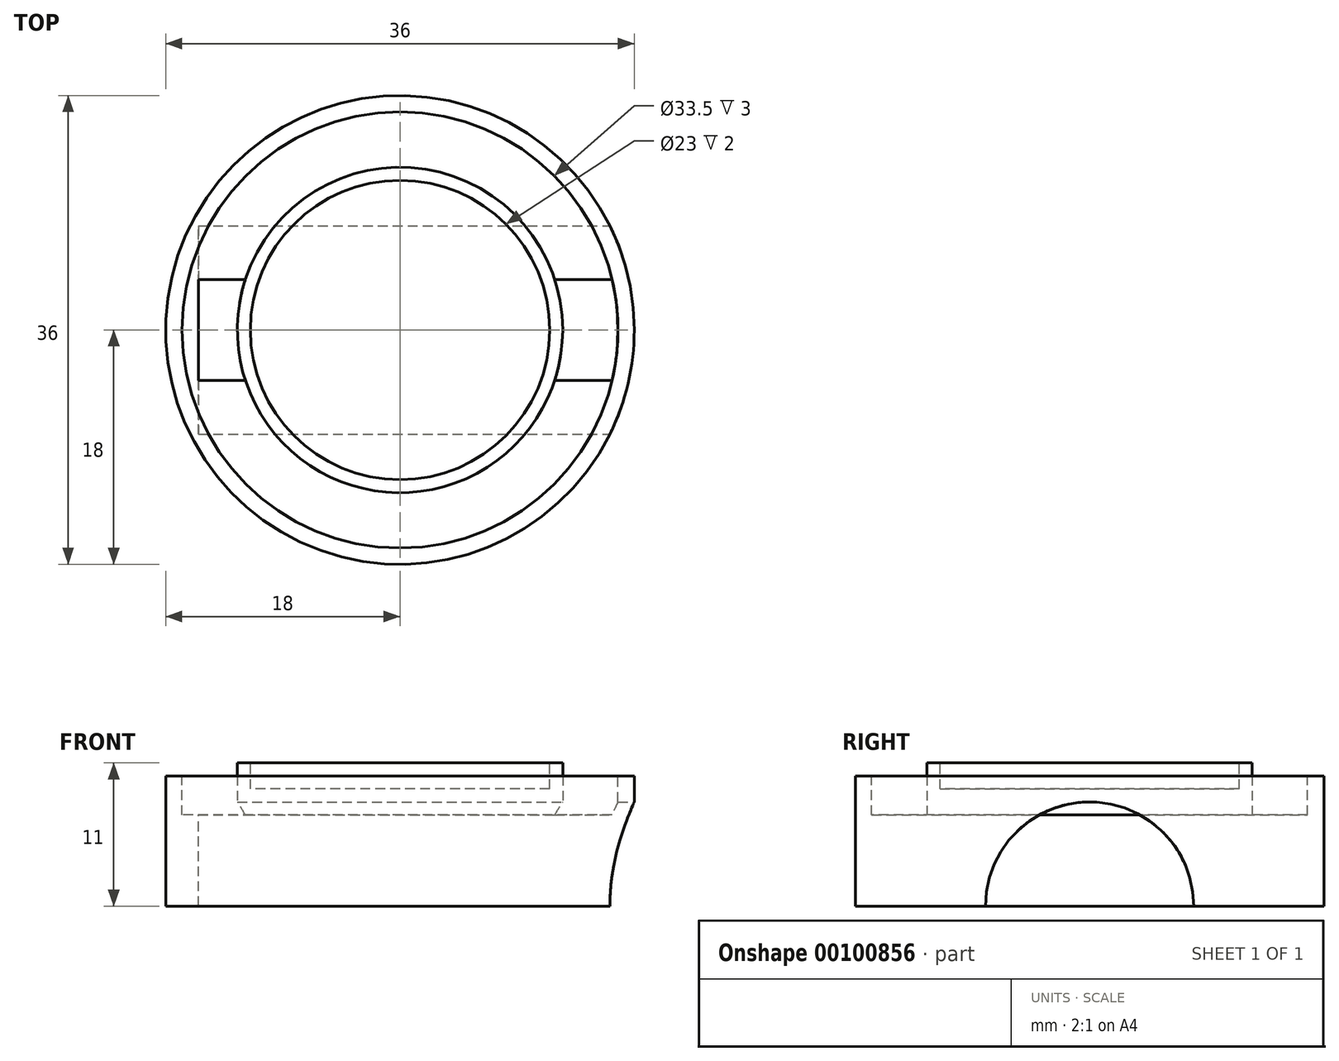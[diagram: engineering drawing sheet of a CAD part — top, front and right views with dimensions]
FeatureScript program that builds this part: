
annotation { "Feature Type Name" : "Feature", "Feature Type Description" : "" }
export const myFeature = defineFeature(function(context is Context, id is Id, definition is map)
    precondition{}
    {
        {
            var Q0;
            Q0=qCreatedBy(makeId("Top.planeOp"),FACE);
            var sketch = newSketch(context, id + "F0", { "sketchPlane" : qUnion([Q0])});
            skCircle(sketch, "E0", {"center": v(0, 0) * mm, "radius": 18 * mm});
            skCircle(sketch, "E1", {"center": v(0, 0) * mm, "radius": 16.75 * mm});
            skCircle(sketch, "E2", {"center": v(0, 0) * mm, "radius": 12.5 * mm});
            skCircle(sketch, "E3", {"center": v(0, 0) * mm, "radius": 11.5 * mm});
            skSolve(sketch);
        }
        {
            var Q0;
            Q0=makeQuery(id+"F0.imprint","IMPRINT",FACE,{"disambiguationData":[TD([[makeQuery(id+"F0.imprint","IMPRINT",EDGE,{"derivedFrom":sQuery(id+"F0.wireOp",EDGE,"E0")}),1.0]])]});
            var Q1;
            Q1=makeQuery(id+"F0.imprint","IMPRINT",FACE,{"disambiguationData":[TD([[makeQuery(id+"F0.imprint","IMPRINT",EDGE,{"derivedFrom":sQuery(id+"F0.wireOp",EDGE,"E1")}),1.0]])]});
            var Q2;
            Q2=makeQuery(id+"F0.imprint","IMPRINT",FACE,{"disambiguationData":[TD([[makeQuery(id+"F0.imprint","IMPRINT",EDGE,{"derivedFrom":sQuery(id+"F0.wireOp",EDGE,"E3")}),1.0]])]});
            var Q3;
            Q3=makeQuery(id+"F0.imprint","IMPRINT",FACE,{"disambiguationData":[TD([[makeQuery(id+"F0.imprint","IMPRINT",EDGE,{"derivedFrom":sQuery(id+"F0.wireOp",EDGE,"E2")}),1.0]])]});
            extrude(context, id + "F1", {"entities" : qUnion([Q0, Q1, Q2, Q3]), "depth" : 10 * mm});
        }
        {
            var Q0;
            Q0=makeQuery(id+"F1.opExtrude","CAP_FACE",FACE,{"disambiguationData":[OSD([sQuery(id+"F0.wireOp",EDGE,"E0")])],"isStart":false});
            var sketch = newSketch(context, id + "F2", { "sketchPlane" : qUnion([Q0])});
            skCircle(sketch, "E4", {"center": v(0, 0) * mm, "radius": 16.75 * mm});
            skSolve(sketch);
        }
        {
            var Q0;
            Q0=makeQuery(id+"F2.imprint","IMPRINT",FACE,{"disambiguationData":[TD([[makeQuery(id+"F2.imprint","IMPRINT",EDGE,{"derivedFrom":sQuery(id+"F2.wireOp",EDGE,"E4")}),1.0]])]});
            extrude(context, id + "F3", {"entities" : qUnion([Q0]), "operationType" : NewBodyOperationType.REMOVE, "oppositeDirection" : true, "depth" : 3 * mm});
        }
        {
            var Q0;
            Q0=makeQuery(id+"F3.boolean.opBoolean","COPY",FACE,{"derivedFrom":makeQuery(id+"F3.opExtrude","CAP_FACE",FACE,{"disambiguationData":[OSD([sQuery(id+"F2.wireOp",EDGE,"E4")])],"isStart":false})});
            var sketch = newSketch(context, id + "F4", { "sketchPlane" : qUnion([Q0])});
            skCircle(sketch, "E5", {"center": v(0, 0) * mm, "radius": 12.5 * mm});
            skSolve(sketch);
        }
        {
            var Q0;
            Q0=makeQuery(id+"F4.imprint","IMPRINT",FACE,{"disambiguationData":[TD([[makeQuery(id+"F4.imprint","IMPRINT",EDGE,{"derivedFrom":sQuery(id+"F4.wireOp",EDGE,"E5")}),1.0]])]});
            var Q1;
            Q1=sQuery(id+"F4.wireOp",EDGE,"E5");
            extrude(context, id + "F5", {"entities" : qUnion([Q0]), "operationType" : NewBodyOperationType.ADD, "surfaceEntities" : qUnion([Q1]), "depth" : 4 * mm});
        }
        {
            var Q0;
            Q0=makeQuery(id+"F5.opExtrude","CAP_FACE",FACE,{"disambiguationData":[OSD([sQuery(id+"F4.wireOp",EDGE,"E5")])],"isStart":false});
            var sketch = newSketch(context, id + "F6", { "sketchPlane" : qUnion([Q0])});
            skCircle(sketch, "E6", {"center": v(0, 0) * mm, "radius": 11.5 * mm});
            skSolve(sketch);
        }
        {
            var Q0;
            Q0=makeQuery(id+"F6.imprint","IMPRINT",FACE,{"disambiguationData":[TD([[makeQuery(id+"F6.imprint","IMPRINT",EDGE,{"derivedFrom":sQuery(id+"F6.wireOp",EDGE,"E6")}),1.0]])]});
            extrude(context, id + "F7", {"entities" : qUnion([Q0]), "operationType" : NewBodyOperationType.REMOVE, "oppositeDirection" : true, "depth" : 2 * mm});
        }
        {
            var Q0;
            Q0=qCreatedBy(makeId("Right.planeOp"),FACE);
            cPlane(context, id + "F8", {"entities" : qUnion([Q0]), "cplaneType" : CPlaneType.OFFSET, "offset" : 18 * mm, "width" : 150 * mm, "height" : 150 * mm});
        }
        {
            var Q0;
            Q0=qCreatedBy(id+"F8.planeOp",FACE);
            var sketch = newSketch(context, id + "F9", { "sketchPlane" : qUnion([Q0])});
            skCircle(sketch, "E7", {"center": v(0, 0) * mm, "radius": 8 * mm});
            skSolve(sketch);
        }
        {
            var Q0;
            Q0=makeQuery(id+"F9.imprint","IMPRINT",FACE,{"disambiguationData":[TD([[makeQuery(id+"F9.imprint","IMPRINT",EDGE,{"derivedFrom":sQuery(id+"F9.wireOp",EDGE,"E7")}),1.0]])]});
            extrude(context, id + "F10", {"entities" : qUnion([Q0]), "operationType" : NewBodyOperationType.REMOVE, "oppositeDirection" : true, "depth" : 33.5 * mm});
        }
        {
            var Q0;
            Q0=qCreatedBy(id+"F8.planeOp",FACE);
            cPlane(context, id + "F11", {"entities" : qUnion([Q0]), "cplaneType" : CPlaneType.OFFSET, "offset" : 1 * mm, "oppositeDirection" : true, "width" : 150 * mm, "height" : 150 * mm});
        }
        {
            var Q0;
            Q0=qCreatedBy(id+"F11.planeOp",FACE);
            var sketch = newSketch(context, id + "F12", { "sketchPlane" : qUnion([Q0])});
            skArc(sketch, "E8", {"start": v(4.08, 6.88) * mm, "mid": v(0, 8) * mm, "end": v(-4.08, 6.88) * mm});
            skArc(sketch, "E9", {"start": v(4.75, 6.88) * mm, "mid": v(0, 8.36) * mm, "end": v(-4.75, 6.88) * mm});
            skLineSegment(sketch, "E10", {"start": v(-4.75, 6.88) * mm, "end": v(-4.08, 6.88) * mm});
            skLineSegment(sketch, "E11.MirrorCS", {"start": v(4.75, 6.88) * mm, "end": v(4.08, 6.88) * mm});
            skSolve(sketch);
        }
        {
            var Q0;
            Q0=sQuery(id+"F12.wireOp",EDGE,"E8");
            var Q1;
            Q1=sQuery(id+"F12.wireOp",EDGE,"E9");
            var Q2;
            Q2=sQuery(id+"F12.wireOp",EDGE,"E11.MirrorCS");
            var Q3;
            Q3=sQuery(id+"F12.wireOp",EDGE,"E10");
            extrude(context, id + "F13", {"bodyType" : ToolBodyType.SURFACE, "surfaceEntities" : qUnion([Q0, Q1, Q2, Q3]), "oppositeDirection" : true, "depth" : 33.81 * mm});
        }
    });
